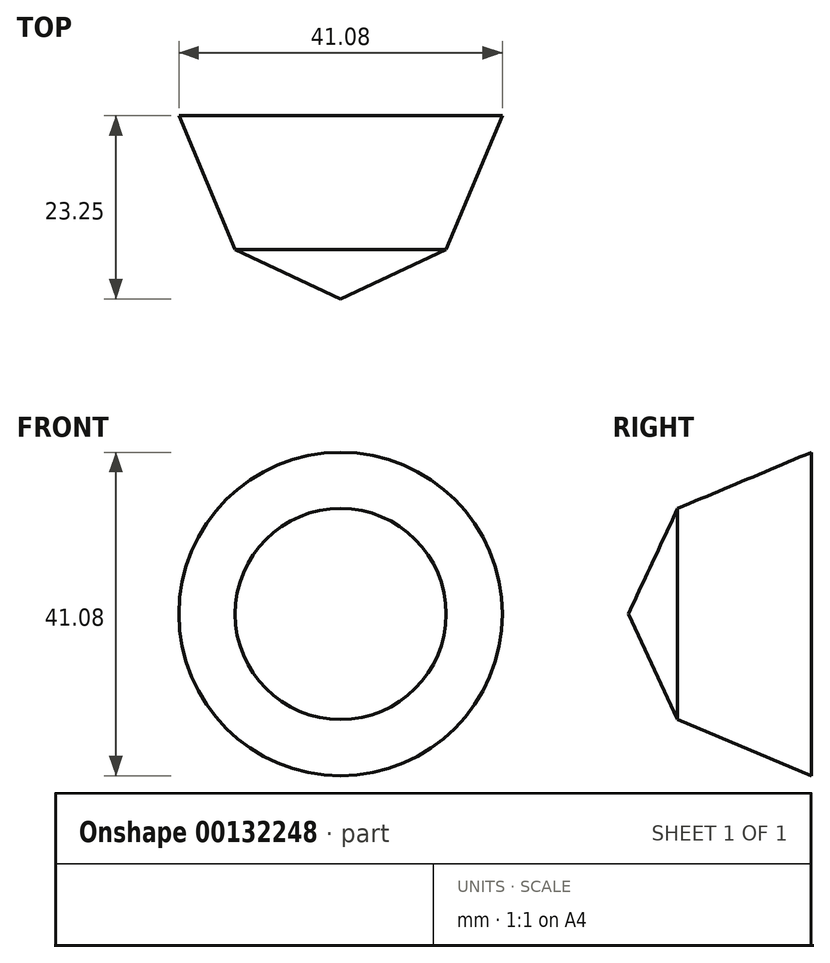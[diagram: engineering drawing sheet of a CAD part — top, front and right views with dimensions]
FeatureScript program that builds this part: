
annotation { "Feature Type Name" : "Feature", "Feature Type Description" : "" }
export const myFeature = defineFeature(function(context is Context, id is Id, definition is map)
    precondition{}
    {
        {
            var Q0;
            Q0=qCreatedBy(makeId("Top.planeOp"),FACE);
            var sketch = newSketch(context, id + "F0", { "sketchPlane" : qUnion([Q0])});
            skLineSegment(sketch, "E0", {"start": v(0, -23.25) * mm, "end": v(13.4, -16.97) * mm});
            skLineSegment(sketch, "E1", {"start": v(13.4, -16.97) * mm, "end": v(20.54, 0) * mm});
            skLineSegment(sketch, "E2", {"start": v(20.54, 0) * mm, "end": v(0, 0) * mm});
            skLineSegment(sketch, "E3", {"start": v(0, 0) * mm, "end": v(0, -23.25) * mm});
            skSolve(sketch);
        }
        {
            var Q0;
            Q0=makeQuery(id+"F0.imprint","IMPRINT",FACE,{"disambiguationData":[TD([[makeQuery(id+"F0.imprint","IMPRINT",EDGE,{"derivedFrom":sQuery(id+"F0.wireOp",EDGE,"E0")}),1.0]])]});
            var Q1;
            Q1=sQuery(id+"F0.wireOp",EDGE,"E3");
            revolve(context, id + "F1", {"entities" : qUnion([Q0]), "axis" : qUnion([Q1]), "revolveType" : RevolveType.FULL});
        }
    });
